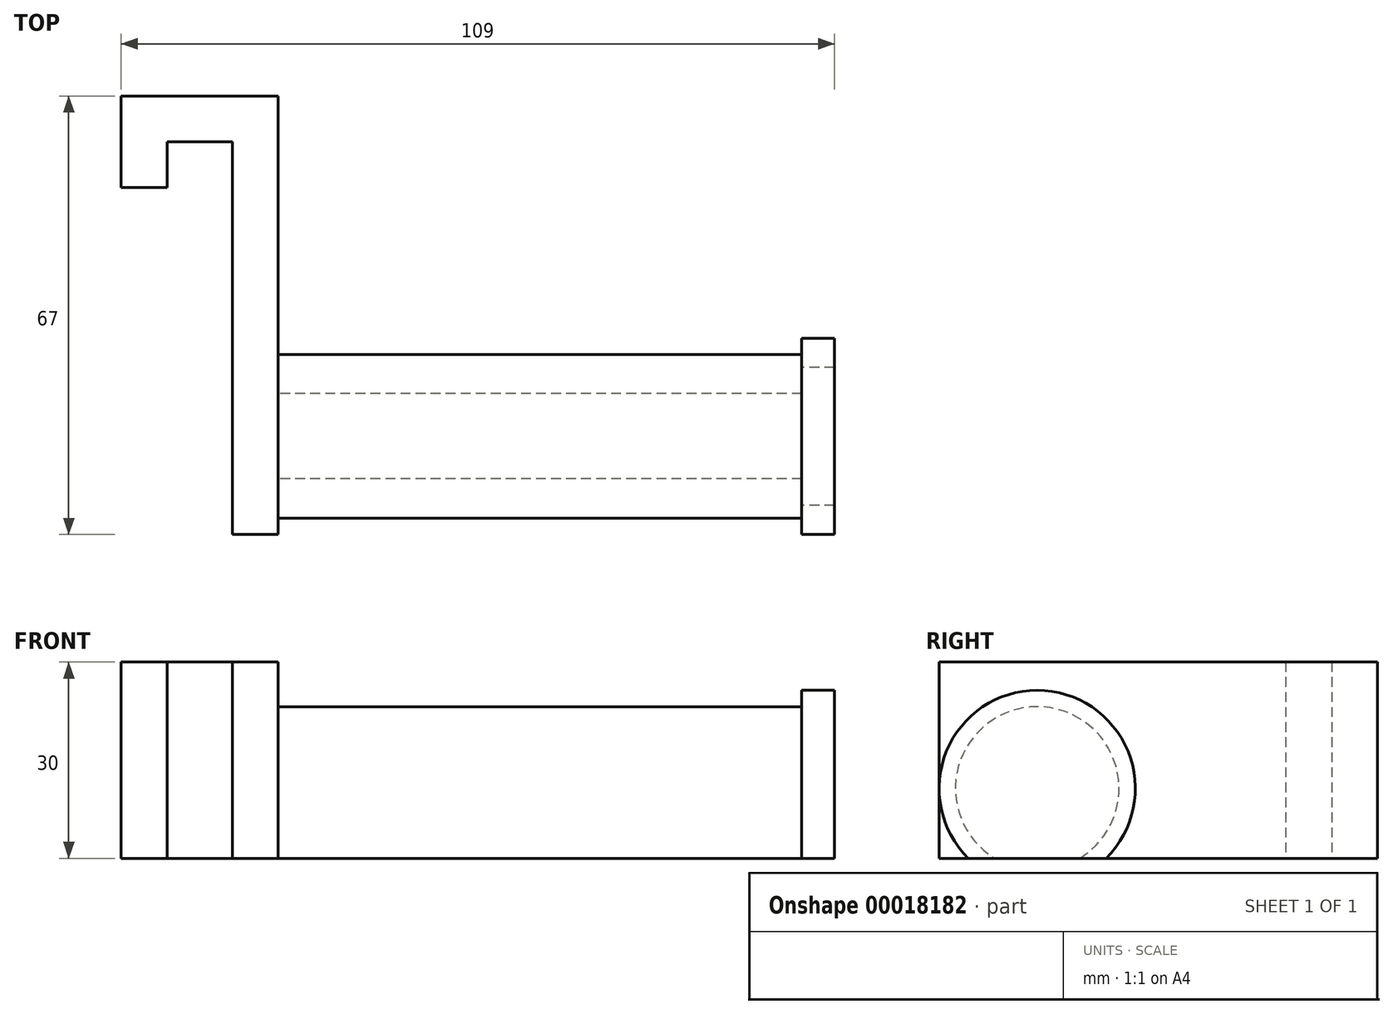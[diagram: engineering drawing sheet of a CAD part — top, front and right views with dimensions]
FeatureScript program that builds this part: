
annotation { "Feature Type Name" : "Feature", "Feature Type Description" : "" }
export const myFeature = defineFeature(function(context is Context, id is Id, definition is map)
    precondition{}
    {
        {
            var Q0;
            Q0=qCreatedBy(makeId("Top.planeOp"),FACE);
            var sketch = newSketch(context, id + "F0", { "sketchPlane" : qUnion([Q0])});
            skLineSegment(sketch, "E0.bottom", {"start": v(-11.94, 32.95) * mm, "end": v(12.06, 32.95) * mm});
            skLineSegment(sketch, "E0.top", {"start": v(5.06, -34.05) * mm, "end": v(12.06, -34.05) * mm});
            skLineSegment(sketch, "E0.left", {"start": v(-11.94, 32.95) * mm, "end": v(-11.94, 18.95) * mm});
            skLineSegment(sketch, "E0.right", {"start": v(12.06, 32.95) * mm, "end": v(12.06, -34.05) * mm});
            skLineSegment(sketch, "E1.top", {"start": v(-4.94, 25.95) * mm, "end": v(5.06, 25.95) * mm});
            skLineSegment(sketch, "E1.left", {"start": v(-4.94, 18.95) * mm, "end": v(-4.94, 25.95) * mm});
            skLineSegment(sketch, "E1.right", {"start": v(5.06, -34.47) * mm, "end": v(5.06, 25.95) * mm});
            skLineSegment(sketch, "E2", {"start": v(-11.94, 18.95) * mm, "end": v(-4.94, 18.95) * mm});
            skSolve(sketch);
        }
        {
            var Q0;
            Q0=makeQuery(id+"F0.imprint","IMPRINT",FACE,{"disambiguationData":[TD([[makeQuery(id+"F0.imprint","IMPRINT",EDGE,{"derivedFrom":sQuery(id+"F0.wireOp",EDGE,"E0.bottom")}),-1.0]])]});
            extrude(context, id + "F1", {"entities" : qUnion([Q0]), "depth" : 30 * mm});
        }
        {
            var Q0;
            Q0=makeQuery(id+"F1.opExtrude","SWEPT_FACE",FACE,{"disambiguationData":[OSD([sQuery(id+"F0.wireOp",EDGE,"E0.right")])]});
            var sketch = newSketch(context, id + "F2", { "sketchPlane" : qUnion([Q0])});
            skLineSegment(sketch, "E3", {"start": v(-19.05, 38.35) * mm, "end": v(-19.05, -8.31) * mm, "construction": true});
            skCircle(sketch, "E4", {"center": v(-19.05, 10.67) * mm, "radius": 12.5 * mm});
            skSolve(sketch);
        }
        {
            var Q0;
            {var subQ0=sQuery(id+"F2.wireOp",EDGE,"E4");var subQ1=makeQuery(id+"F1.opExtrude","CAP_EDGE",EDGE,{"disambiguationData":[OSD([sQuery(id+"F0.wireOp",EDGE,"E0.right")])],"isStart":true});var subQ2=makeQuery(id+"F2.imprint","INTERSECT",VERTEX,{"disambiguationData":[OD(0.0)],"derivedFrom":[subQ1,subQ0]});Q0=makeQuery(id+"F2.imprint","IMPRINT",FACE,{"disambiguationData":[TD([[makeQuery(id+"F2.imprint","IMPRINT",EDGE,{"disambiguationData":[TD([[subQ2,-1.0]])],"derivedFrom":subQ0}),1.0]])]});}
            var Q1;
            Q1=sQuery(id+"F2.wireOp",EDGE,"E4");
            extrude(context, id + "F3", {"entities" : qUnion([Q0]), "operationType" : NewBodyOperationType.ADD, "surfaceEntities" : qUnion([Q1]), "depth" : 80 * mm});
        }
        {
            var Q0;
            Q0=makeQuery(id+"F3.opExtrude","CAP_FACE",FACE,{"disambiguationData":[OSD([sQuery(id+"F0.wireOp",EDGE,"E0.right"),sQuery(id+"F2.wireOp",EDGE,"E4")])],"isStart":false});
            var sketch = newSketch(context, id + "F4", { "sketchPlane" : qUnion([Q0])});
            skArc(sketch, "E5", {"start": v(-8.51, 0) * mm, "mid": v(-19.05, 25.67) * mm, "end": v(-29.6, 0) * mm});
            skLineSegment(sketch, "E6", {"start": v(-29.6, 0) * mm, "end": v(-8.51, 0) * mm});
            skSolve(sketch);
        }
        {
            var Q0;
            Q0=makeQuery(id+"F4.imprint","IMPRINT",FACE,{"disambiguationData":[TD([[makeQuery(id+"F4.imprint","IMPRINT",EDGE,{"derivedFrom":sQuery(id+"F4.wireOp",EDGE,"E5")}),1.0]])]});
            var Q1;
            Q1=makeQuery(id+"F4.imprint","IMPRINT",FACE,{"disambiguationData":[TD([[makeQuery(id+"F4.imprint","IMPRINT",EDGE,{"derivedFrom":makeQuery(id+"F3.opExtrude","CAP_EDGE",EDGE,{"disambiguationData":[OSD([sQuery(id+"F2.wireOp",EDGE,"E4")])],"isStart":false})}),1.0]])]});
            var Q2;
            Q2=sQuery(id+"F4.wireOp",EDGE,"E5");
            extrude(context, id + "F5", {"entities" : qUnion([Q0, Q1]), "operationType" : NewBodyOperationType.ADD, "surfaceEntities" : qUnion([Q2]), "depth" : 5 * mm});
        }
    });
